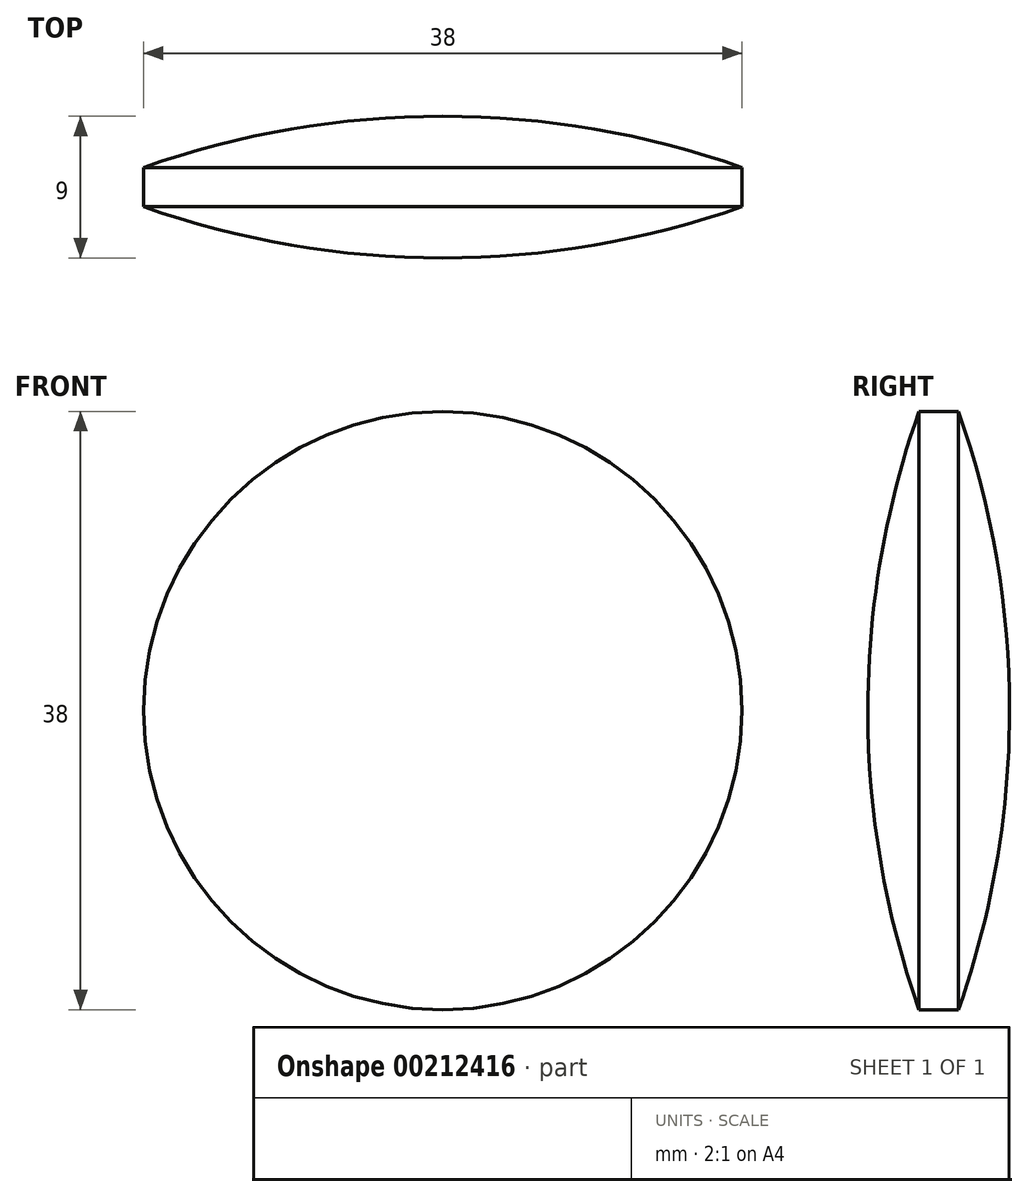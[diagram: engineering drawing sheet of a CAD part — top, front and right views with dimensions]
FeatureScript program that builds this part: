
annotation { "Feature Type Name" : "Feature", "Feature Type Description" : "" }
export const myFeature = defineFeature(function(context is Context, id is Id, definition is map)
    precondition{}
    {
        {
            var Q0;
            Q0=qCreatedBy(makeId("Right.planeOp"),FACE);
            var sketch = newSketch(context, id + "F0", { "sketchPlane" : qUnion([Q0])});
            skLineSegment(sketch, "E0.bottom", {"start": v(-1.25, 19) * mm, "end": v(1.25, 19) * mm});
            skLineSegment(sketch, "E0.left", {"start": v(-1.25, 19) * mm, "end": v(-1.25, -19) * mm, "construction": true});
            skLineSegment(sketch, "E0.right", {"start": v(1.25, 19) * mm, "end": v(1.25, -19) * mm, "construction": true});
            skArc(sketch, "E1", {"start": v(-1.25, 19) * mm, "mid": v(-3.68, 9.64) * mm, "end": v(-4.5, 0) * mm});
            skArc(sketch, "E2", {"start": v(4.5, 0) * mm, "mid": v(3.68, 9.64) * mm, "end": v(1.25, 19) * mm});
            skLineSegment(sketch, "E3", {"start": v(-4.5, 0) * mm, "end": v(4.5, 0) * mm});
            skSolve(sketch);
        }
        {
            var Q0;
            Q0=qSketchRegion(id+"F0",true);
            var Q1;
            Q1=sQuery(id+"F0.wireOp",EDGE,"E3");
            revolve(context, id + "F1", {"entities" : qUnion([Q0]), "axis" : qUnion([Q1]), "revolveType" : RevolveType.FULL});
        }
    });
